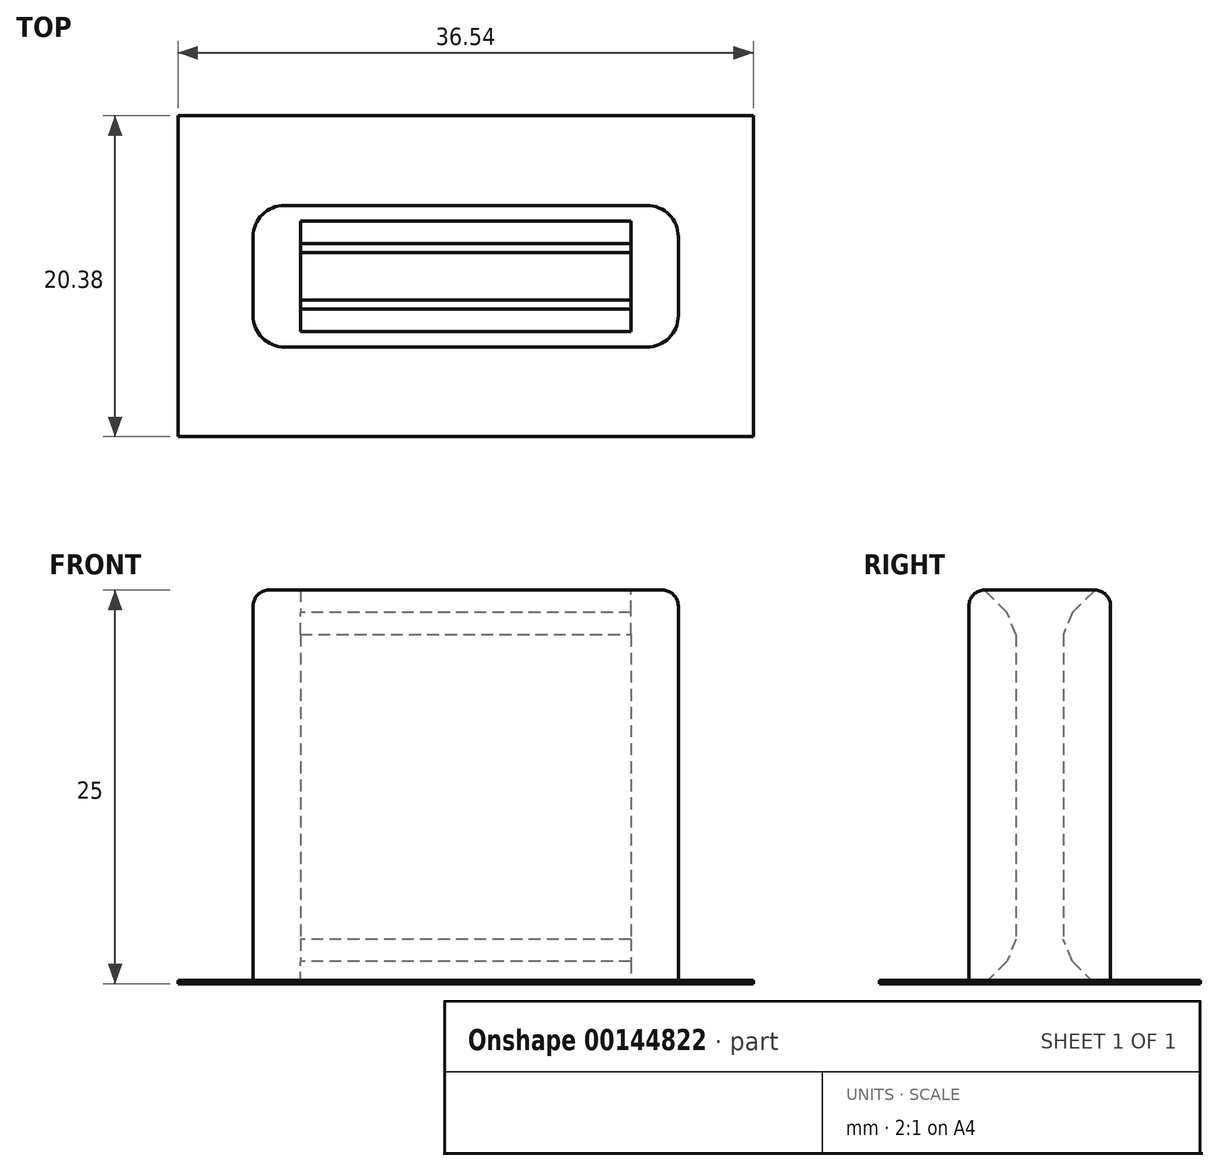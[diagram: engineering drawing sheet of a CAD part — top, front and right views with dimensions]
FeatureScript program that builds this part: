
annotation { "Feature Type Name" : "Feature", "Feature Type Description" : "" }
export const myFeature = defineFeature(function(context is Context, id is Id, definition is map)
    precondition{}
    {
        {
            var Q0;
            Q0=qCreatedBy(makeId("Top.planeOp"),FACE);
            var sketch = newSketch(context, id + "F0", { "sketchPlane" : qUnion([Q0])});
            skLineSegment(sketch, "E0.bottom", {"start": v(10.5, -1.5) * mm, "end": v(-10.5, -1.5) * mm});
            skLineSegment(sketch, "E0.top", {"start": v(10.5, 1.5) * mm, "end": v(-10.5, 1.5) * mm});
            skLineSegment(sketch, "E0.left", {"start": v(10.5, -1.5) * mm, "end": v(10.5, 1.5) * mm});
            skLineSegment(sketch, "E0.right", {"start": v(-10.5, -1.5) * mm, "end": v(-10.5, 1.5) * mm});
            skPoint(sketch, "E0.middle", {"position": v(0, 0) * mm});
            skLineSegment(sketch, "E1.bottom", {"start": v(11.5, -4.5) * mm, "end": v(-11.5, -4.5) * mm});
            skLineSegment(sketch, "E1.top", {"start": v(11.5, 4.5) * mm, "end": v(-11.5, 4.5) * mm});
            skLineSegment(sketch, "E1.left", {"start": v(13.5, -2.5) * mm, "end": v(13.5, 2.5) * mm});
            skLineSegment(sketch, "E1.right", {"start": v(-13.5, -2.5) * mm, "end": v(-13.5, 2.5) * mm});
            skPoint(sketch, "E2.visualSharp", {"position": v(-13.5, 4.5) * mm});
            skArc(sketch, "E2.filletArc", {"start": v(-11.5, 4.5) * mm, "mid": v(-12.91, 3.91) * mm, "end": v(-13.5, 2.5) * mm});
            skPoint(sketch, "E3.visualSharp", {"position": v(-13.5, -4.5) * mm});
            skArc(sketch, "E3.filletArc", {"start": v(-13.5, -2.5) * mm, "mid": v(-12.91, -3.91) * mm, "end": v(-11.5, -4.5) * mm});
            skPoint(sketch, "E4.visualSharp", {"position": v(13.5, -4.5) * mm});
            skArc(sketch, "E4.filletArc", {"start": v(11.5, -4.5) * mm, "mid": v(12.91, -3.91) * mm, "end": v(13.5, -2.5) * mm});
            skPoint(sketch, "E5.visualSharp", {"position": v(13.5, 4.5) * mm});
            skArc(sketch, "E5.filletArc", {"start": v(13.5, 2.5) * mm, "mid": v(12.91, 3.91) * mm, "end": v(11.5, 4.5) * mm});
            skLineSegment(sketch, "E6.bottom", {"start": v(18.27, -10.2) * mm, "end": v(-18.27, -10.2) * mm});
            skLineSegment(sketch, "E6.top", {"start": v(18.27, 10.2) * mm, "end": v(-18.27, 10.2) * mm});
            skLineSegment(sketch, "E6.left", {"start": v(18.27, -10.2) * mm, "end": v(18.27, 10.2) * mm});
            skLineSegment(sketch, "E6.right", {"start": v(-18.27, -10.2) * mm, "end": v(-18.27, 10.2) * mm});
            skSolve(sketch);
        }
        {
            var Q0;
            Q0=makeQuery(id+"F0.imprint","IMPRINT",FACE,{"disambiguationData":[TD([[makeQuery(id+"F0.imprint","IMPRINT",EDGE,{"derivedFrom":sQuery(id+"F0.wireOp",EDGE,"E0.bottom")}),1.0]])]});
            extrude(context, id + "F1", {"entities" : qUnion([Q0]), "depth" : 25 * mm});
        }
        {
            var Q0;
            Q0=makeQuery(id+"F1.opExtrude","CAP_EDGE",EDGE,{"disambiguationData":[OSD([sQuery(id+"F0.wireOp",EDGE,"E0.bottom")])],"isStart":false});
            var Q1;
            Q1=makeQuery(id+"F1.opExtrude","CAP_EDGE",EDGE,{"disambiguationData":[OSD([sQuery(id+"F0.wireOp",EDGE,"E0.top")])],"isStart":false});
            var Q2;
            Q2=makeQuery(id+"F1.opExtrude","CAP_EDGE",EDGE,{"disambiguationData":[OSD([sQuery(id+"F0.wireOp",EDGE,"E0.top")])],"isStart":true});
            var Q3;
            Q3=makeQuery(id+"F1.opExtrude","CAP_EDGE",EDGE,{"disambiguationData":[OSD([sQuery(id+"F0.wireOp",EDGE,"E0.bottom")])],"isStart":true});
            chamfer(context, id + "F2", {"entities" : qUnion([Q0, Q1, Q2, Q3]), "width" : 2 * mm, "tangentPropagation" : true});
        }
        {
            var Q0;
            {var subQ0=sQuery(id+"F0.wireOp",EDGE,"E0.top");Q0=makeQuery(id+"F2.opChamfer","BLEND_EDGE",EDGE,{"blendedFrom":[makeQuery(id+"F1.opExtrude","CAP_EDGE",EDGE,{"disambiguationData":[OSD([subQ0])],"isStart":false}),makeQuery(id+"F1.opExtrude","SWEPT_FACE",FACE,{"disambiguationData":[OSD([subQ0])]})],"blendedInto":[makeQuery(id+"F1.opExtrude","SWEPT_FACE",FACE,{"disambiguationData":[OSD([subQ0])]})]});}
            var Q1;
            {var subQ0=sQuery(id+"F0.wireOp",EDGE,"E0.bottom");Q1=makeQuery(id+"F2.opChamfer","BLEND_EDGE",EDGE,{"blendedFrom":[makeQuery(id+"F1.opExtrude","CAP_EDGE",EDGE,{"disambiguationData":[OSD([subQ0])],"isStart":false}),makeQuery(id+"F1.opExtrude","SWEPT_FACE",FACE,{"disambiguationData":[OSD([subQ0])]})],"blendedInto":[makeQuery(id+"F1.opExtrude","SWEPT_FACE",FACE,{"disambiguationData":[OSD([subQ0])]})]});}
            var Q2;
            {var subQ0=sQuery(id+"F0.wireOp",EDGE,"E0.bottom");Q2=makeQuery(id+"F2.opChamfer","BLEND_EDGE",EDGE,{"blendedFrom":[makeQuery(id+"F1.opExtrude","CAP_EDGE",EDGE,{"disambiguationData":[OSD([subQ0])],"isStart":true}),makeQuery(id+"F1.opExtrude","SWEPT_FACE",FACE,{"disambiguationData":[OSD([subQ0])]})],"blendedInto":[makeQuery(id+"F1.opExtrude","SWEPT_FACE",FACE,{"disambiguationData":[OSD([subQ0])]})]});}
            var Q3;
            {var subQ0=sQuery(id+"F0.wireOp",EDGE,"E0.top");Q3=makeQuery(id+"F2.opChamfer","BLEND_EDGE",EDGE,{"blendedFrom":[makeQuery(id+"F1.opExtrude","CAP_EDGE",EDGE,{"disambiguationData":[OSD([subQ0])],"isStart":true}),makeQuery(id+"F1.opExtrude","SWEPT_FACE",FACE,{"disambiguationData":[OSD([subQ0])]})],"blendedInto":[makeQuery(id+"F1.opExtrude","SWEPT_FACE",FACE,{"disambiguationData":[OSD([subQ0])]})]});}
            chamfer(context, id + "F3", {"entities" : qUnion([Q0, Q1, Q2, Q3]), "width" : 2 * mm, "tangentPropagation" : true});
        }
        {
            var Q0;
            Q0=makeQuery(id+"F1.opExtrude","CAP_EDGE",EDGE,{"disambiguationData":[OSD([sQuery(id+"F0.wireOp",EDGE,"E1.top")])],"isStart":false});
            fillet(context, id + "F4", {"entities" : qUnion([Q0]), "radius" : 1 * mm, "tangentPropagation" : true, "allowEdgeOverflow" : false});
        }
        {
            var Q0;
            Q0=makeQuery(id+"F0.imprint","IMPRINT",FACE,{"disambiguationData":[TD([[makeQuery(id+"F0.imprint","IMPRINT",EDGE,{"derivedFrom":sQuery(id+"F0.wireOp",EDGE,"E1.bottom")}),1.0]])]});
            extrude(context, id + "F5", {"entities" : qUnion([Q0]), "operationType" : NewBodyOperationType.ADD, "depth" : 0.2 * mm});
        }
    });
